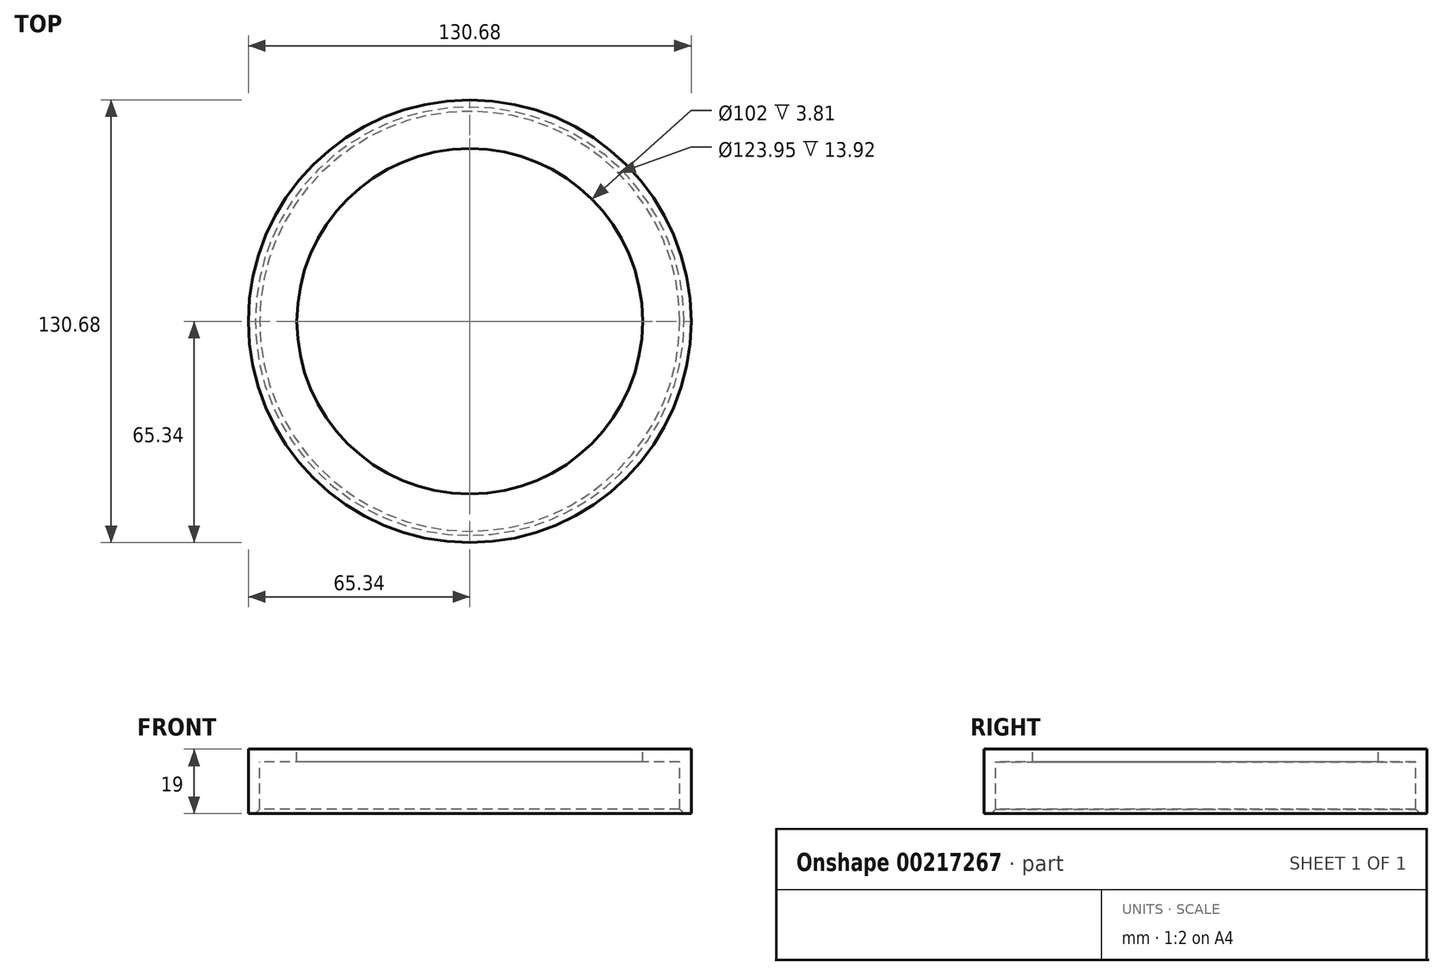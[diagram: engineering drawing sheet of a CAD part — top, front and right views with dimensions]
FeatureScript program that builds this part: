
annotation { "Feature Type Name" : "Feature", "Feature Type Description" : "" }
export const myFeature = defineFeature(function(context is Context, id is Id, definition is map)
    precondition{}
    {
        {
            var Q0;
            Q0=qCreatedBy(makeId("Top.planeOp"),FACE);
            var sketch = newSketch(context, id + "F0", { "sketchPlane" : qUnion([Q0])});
            skCircle(sketch, "E0", {"center": v(0, 0) * mm, "radius": 64.77 * mm});
            skCircle(sketch, "E1", {"center": v(0, 0) * mm, "radius": 51 * mm});
            skSolve(sketch);
        }
        {
            var Q0;
            Q0=makeQuery(id+"F0.imprint","IMPRINT",FACE,{"disambiguationData":[TD([[makeQuery(id+"F0.imprint","IMPRINT",EDGE,{"derivedFrom":sQuery(id+"F0.wireOp",EDGE,"E0")}),1.0]])]});
            extrude(context, id + "F1", {"entities" : qUnion([Q0]), "oppositeDirection" : true, "depth" : 3.8 * mm});
        }
        {
            var Q0;
            Q0=makeQuery(id+"F1.opExtrude","CAP_FACE",FACE,{"disambiguationData":[OSD([sQuery(id+"F0.wireOp",EDGE,"E0")])],"isStart":true});
            var sketch = newSketch(context, id + "F2", { "sketchPlane" : qUnion([Q0])});
            skCircle(sketch, "E2", {"center": v(0, 0) * mm, "radius": 65.34 * mm});
            skCircle(sketch, "E3", {"center": v(0, 0) * mm, "radius": 61.98 * mm});
            skSolve(sketch);
        }
        {
            var Q0;
            Q0=qSketchRegion(id+"F2",true);
            extrude(context, id + "F3", {"entities" : qUnion([Q0]), "operationType" : NewBodyOperationType.ADD, "oppositeDirection" : true, "depth" : 19 * mm});
        }
        {
            var Q0;
            Q0=makeQuery(id+"F3.opExtrude","CAP_EDGE",EDGE,{"disambiguationData":[OSD([sQuery(id+"F2.wireOp",EDGE,"E3")])],"isStart":false});
            chamfer(context, id + "F4", {"entities" : qUnion([Q0]), "width" : 1.27 * mm, "tangentPropagation" : true});
        }
    });
